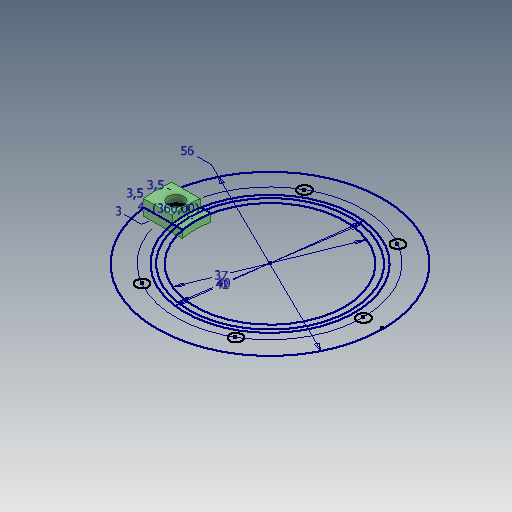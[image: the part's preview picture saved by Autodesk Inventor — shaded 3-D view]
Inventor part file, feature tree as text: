
AUTODESK INVENTOR PART (.ipt)
format: ipt  version: 2020.3 (Build 243373000, 373)  size: 111,616 bytes
history: native  units: mm
features: extrude x2, sketch x1
ambient origin geometry x8: Origin, YZ Plane, XZ Plane, XY Plane, X Axis, Y Axis, Z Axis, Center Point
bodies: Solid1 (feature_tree)
feature tree (3):
  sketch  "Sketch2"  dims[d7=60.0mm d8=37.0mm d9=3.0mm d10=360.0deg d11=56.0mm d12=40.0mm d13=42.0mm d14=3.5mm d15=3.5mm d16=4.0mm d17=1.8mm d18=0.0mm d19=2.0mm d20=0.0mm]
  extrude  "Extrusion1"  Depth=2.0mm
  extrude  "Extrusion2"  Depth=2.0mm
